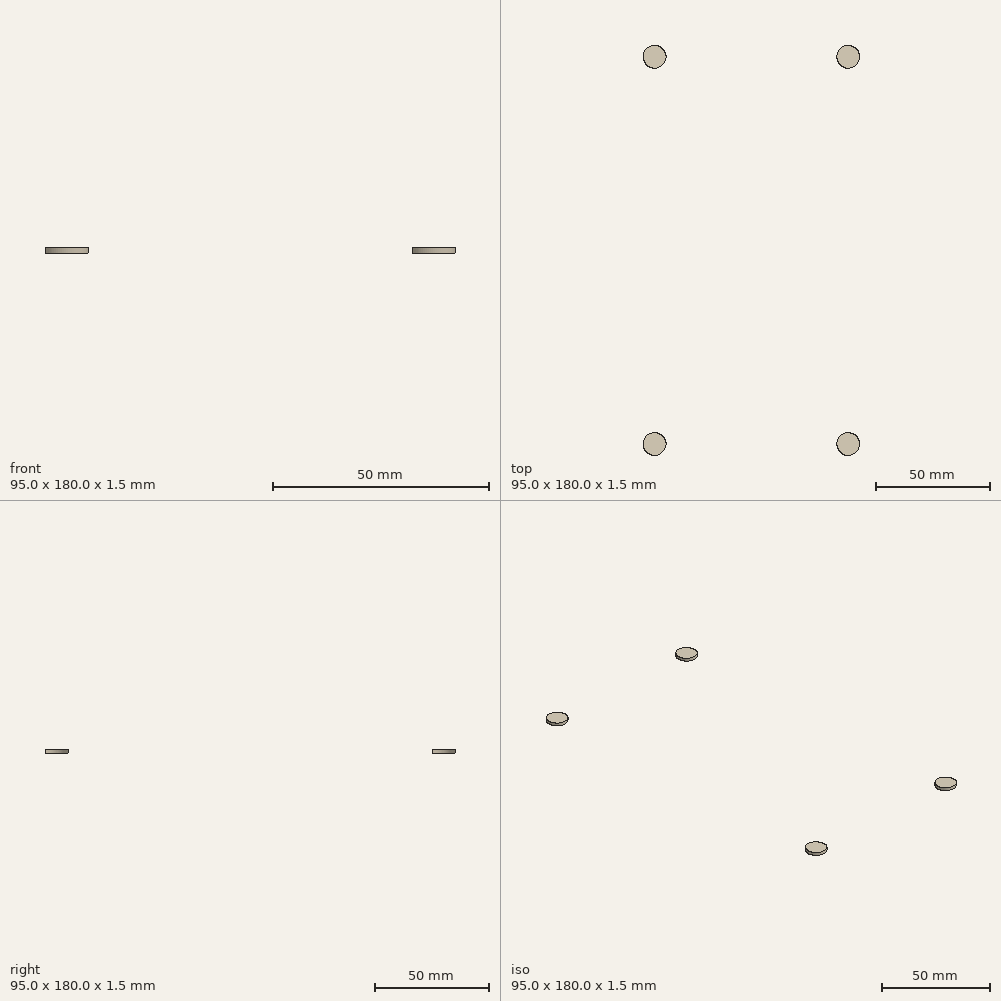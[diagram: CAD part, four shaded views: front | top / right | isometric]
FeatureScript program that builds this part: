
annotation { "Feature Type Name" : "Feature", "Feature Type Description" : "" }
export const myFeature = defineFeature(function(context is Context, id is Id, definition is map)
    precondition{}
    {
        {
            var Q0;
            Q0=qCreatedBy(makeId("Top.planeOp"),FACE);
            var sketch = newSketch(context, id + "F0", { "sketchPlane" : qUnion([Q0])});
            skCircle(sketch, "E0", {"center": v(42.5, -85) * mm, "radius": 5 * mm});
            skCircle(sketch, "E1.MirrorC", {"center": v(-42.5, -85) * mm, "radius": 5 * mm});
            skCircle(sketch, "E2.MirrorC", {"center": v(-42.5, 85) * mm, "radius": 5 * mm});
            skCircle(sketch, "E3.MirrorC", {"center": v(42.5, 85) * mm, "radius": 5 * mm});
            skSolve(sketch);
        }
        {
            var Q0;
            Q0 = qSketchRegion(id + "F0", true);
            extrude(context, id + "F1", {"entities" : qUnion([Q0]), "oppositeDirection" : true, "depth" : 1.5 * mm, "offsetDistance" : 25 * mm});
        }
    });
